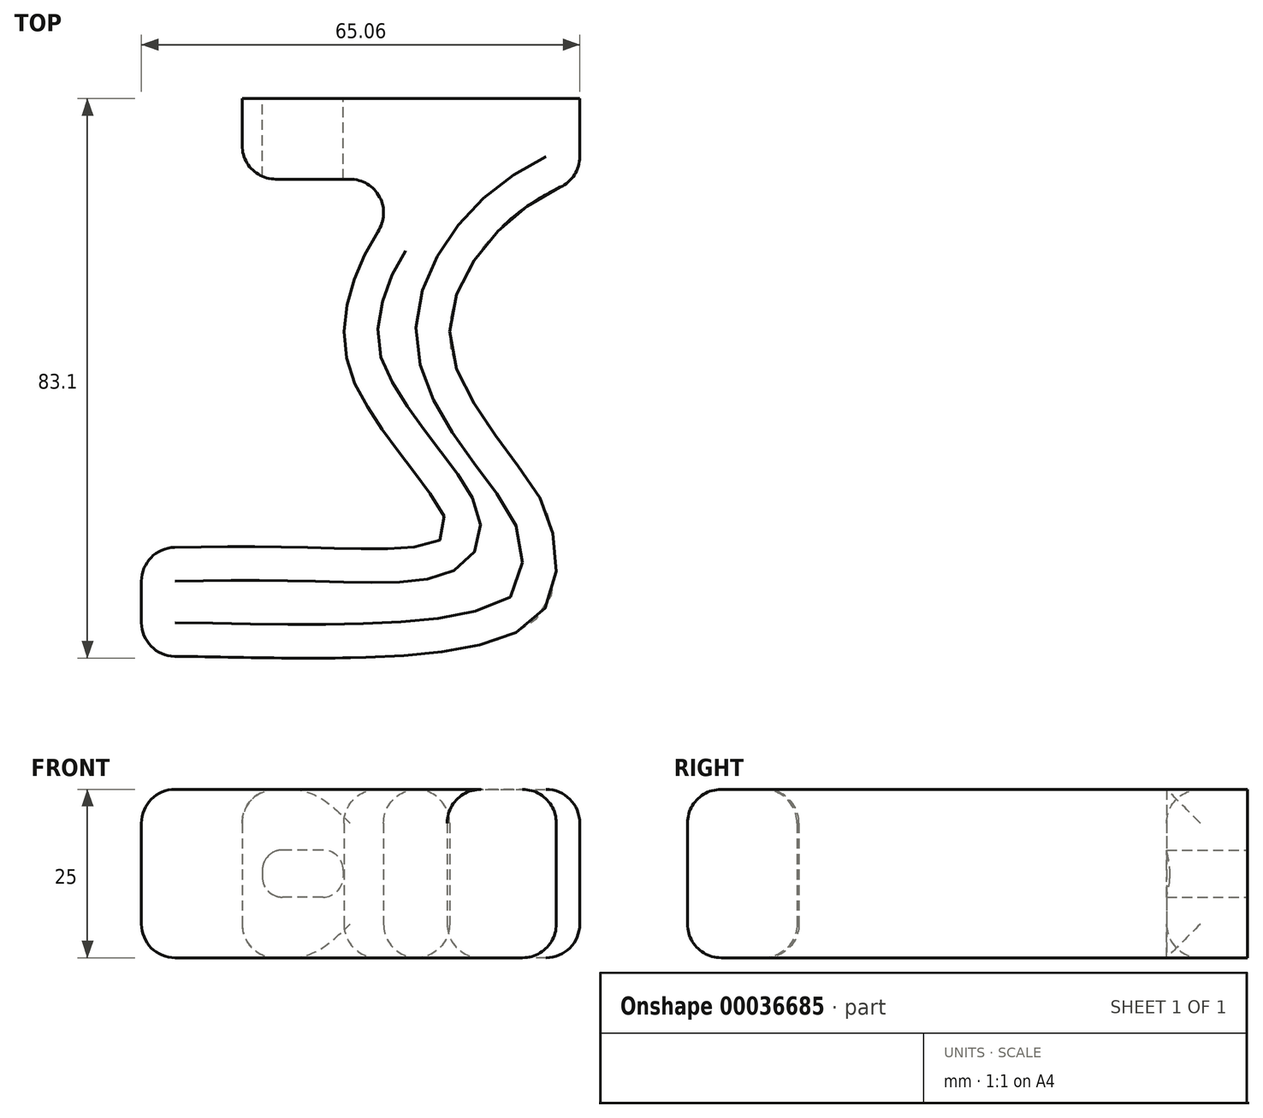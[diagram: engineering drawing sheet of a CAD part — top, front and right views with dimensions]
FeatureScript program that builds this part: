
annotation { "Feature Type Name" : "Feature", "Feature Type Description" : "" }
export const myFeature = defineFeature(function(context is Context, id is Id, definition is map)
    precondition{}
    {
        {
            var Q0;
            Q0=qCreatedBy(makeId("Top.planeOp"),FACE);
            var sketch = newSketch(context, id + "F0", { "sketchPlane" : qUnion([Q0])});
            skFitSpline(sketch, "E0", {"points": [v(6.97, 40.8) * mm, v(-5.98, 24.26) * mm, v(-5.59, 10.99) * mm, v(5.2, -5.06) * mm, v(8.02, -12.1) * mm, v(-1.71, -14.08) * mm, v(-37.05, -14) * mm], "startDerivative": vector(-118.42, -54.77) * mm, "endDerivative": vector(-270.33, -6.71) * mm});
            skLineSegment(sketch, "E1", {"start": v(-37.05, -14) * mm, "end": v(-37.05, -30) * mm});
            skFitSpline(sketch, "E2", {"points": [v(-37.05, -30) * mm, v(21.45, -24.6) * mm, v(24.08, -12.1) * mm, v(21.2, -5.06) * mm, v(10.41, 10.99) * mm, v(9.95, 24.26) * mm, v(28.01, 40.8) * mm], "startDerivative": vector(246.93, -2.05) * mm, "endDerivative": vector(154.82, 54.74) * mm});
            skLineSegment(sketch, "E3", {"start": v(6.97, 40.8) * mm, "end": v(-22.1, 40.8) * mm});
            skLineSegment(sketch, "E4", {"start": v(-22.1, 40.8) * mm, "end": v(-22.1, 52.77) * mm});
            skLineSegment(sketch, "E5", {"start": v(-22.1, 52.77) * mm, "end": v(28.01, 52.77) * mm});
            skLineSegment(sketch, "E6", {"start": v(28.01, 52.77) * mm, "end": v(28.01, 40.8) * mm});
            skSolve(sketch);
        }
        {
            var Q0;
            Q0 = qSketchRegion(id + "F0", true);
            extrude(context, id + "F1", {"entities" : qUnion([Q0]), "depth" : 25 * mm});
        }
        {
            var Q0;
            Q0=makeQuery(id+"F1.opExtrude","SWEPT_FACE",FACE,{"disambiguationData":[OSD([sQuery(id+"F0.wireOp",EDGE,"E0")])]});
            var Q1;
            Q1=makeQuery(id+"F1.opExtrude","SWEPT_FACE",FACE,{"disambiguationData":[OSD([sQuery(id+"F0.wireOp",EDGE,"E2")])]});
            var Q2;
            Q2=makeQuery(id+"F1.opExtrude","CAP_EDGE",EDGE,{"disambiguationData":[OSD([sQuery(id+"F0.wireOp",EDGE,"E6")])],"isStart":false});
            var Q3;
            Q3=makeQuery(id+"F1.opExtrude","CAP_EDGE",EDGE,{"disambiguationData":[OSD([sQuery(id+"F0.wireOp",EDGE,"E6")])],"isStart":true});
            var Q4;
            Q4=makeQuery(id+"F1.opExtrude","CAP_EDGE",EDGE,{"disambiguationData":[OSD([sQuery(id+"F0.wireOp",EDGE,"E4")])],"isStart":false});
            var Q5;
            Q5=makeQuery(id+"F1.opExtrude","CAP_EDGE",EDGE,{"disambiguationData":[OSD([sQuery(id+"F0.wireOp",EDGE,"E4")])],"isStart":true});
            var Q6;
            Q6=makeQuery(id+"F1.opExtrude","SWEPT_EDGE",EDGE,{"disambiguationData":[OSD([sQuery(id+"F0.wireOp",EDGE,"E3"),sQuery(id+"F0.wireOp",EDGE,"E4")])]});
            var Q7;
            Q7=makeQuery(id+"F1.opExtrude","SWEPT_FACE",FACE,{"disambiguationData":[OSD([sQuery(id+"F0.wireOp",EDGE,"E1")])]});
            fillet(context, id + "F2", {"entities" : qUnion([Q0, Q1, Q2, Q3, Q4, Q5, Q6, Q7]), "radius" : 5 * mm, "tangentPropagation" : true, "allowEdgeOverflow" : false});
        }
        {
            var Q0;
            Q0=makeQuery(id+"F1.opExtrude","SWEPT_FACE",FACE,{"disambiguationData":[OSD([sQuery(id+"F0.wireOp",EDGE,"E5")])]});
            var sketch = newSketch(context, id + "F3", { "sketchPlane" : qUnion([Q0])});
            skLineSegment(sketch, "E7.bottom", {"start": v(10.1, 16) * mm, "end": v(16.1, 16) * mm});
            skLineSegment(sketch, "E7.top", {"start": v(10.1, 9) * mm, "end": v(16.1, 9) * mm});
            skLineSegment(sketch, "E7.left", {"start": v(7.1, 13) * mm, "end": v(7.1, 12) * mm});
            skLineSegment(sketch, "E7.right", {"start": v(19.1, 13) * mm, "end": v(19.1, 12) * mm});
            skPoint(sketch, "E8.visualSharp", {"position": v(7.1, 16) * mm});
            skArc(sketch, "E8.filletArc", {"start": v(10.1, 16) * mm, "mid": v(7.99, 15.12) * mm, "end": v(7.1, 13) * mm});
            skPoint(sketch, "E9.visualSharp", {"position": v(19.1, 16) * mm});
            skArc(sketch, "E9.filletArc", {"start": v(19.1, 13) * mm, "mid": v(18.23, 15.12) * mm, "end": v(16.1, 16) * mm});
            skPoint(sketch, "E10.visualSharp", {"position": v(19.1, 9) * mm});
            skArc(sketch, "E10.filletArc", {"start": v(16.1, 9) * mm, "mid": v(18.23, 9.88) * mm, "end": v(19.1, 12) * mm});
            skPoint(sketch, "E11.visualSharp", {"position": v(7.1, 9) * mm});
            skArc(sketch, "E11.filletArc", {"start": v(7.1, 12) * mm, "mid": v(7.99, 9.88) * mm, "end": v(10.1, 9) * mm});
            skSolve(sketch);
        }
        {
            var Q0;
            Q0=makeQuery(id+"F3.imprint","IMPRINT",FACE,{"disambiguationData":[TD([[makeQuery(id+"F3.imprint","IMPRINT",EDGE,{"derivedFrom":sQuery(id+"F3.wireOp",EDGE,"E7.bottom")}),-1.0]])]});
            var Q1;
            Q1=makeQuery(id+"F1.opExtrude","SWEPT_FACE",FACE,{"disambiguationData":[OSD([sQuery(id+"F0.wireOp",EDGE,"E3")])]});
            extrude(context, id + "F4", {"entities" : qUnion([Q0]), "operationType" : NewBodyOperationType.REMOVE, "endBound" : BoundingType.UP_TO_SURFACE, "oppositeDirection" : true, "endBoundEntityFace" : qUnion([Q1]), "depth" : 25 * mm});
        }
    });
